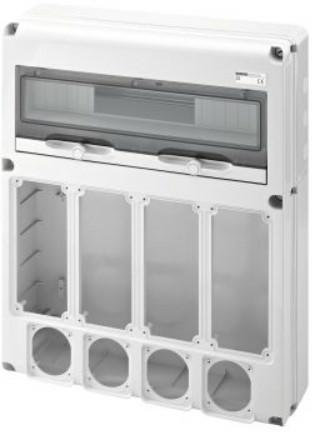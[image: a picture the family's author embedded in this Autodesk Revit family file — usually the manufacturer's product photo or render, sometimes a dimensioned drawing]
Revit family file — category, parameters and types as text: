
# Revit family: Building-IEC309Boards-GEWISS-68QDIN-DISTRIBUTION-BOARD-20MOD_4SOCKET-OUTLETS_IB_VERT_4SOCKET-OUTLETS
name_source: partatom
category: Apparecchi elettrici
units: mm (PartAtom-declared; Revit-internal decimal feet)

## family parameters
Condiviso = No
Host = Superficie
Mantenere orientamento annotazione = Sì
Punto di calcolo locali = Sì
Quota connettore circolare = Usa diametro
Taglio con vuoti quando caricato = No
Tipo di parte = Normale

## types (1)
- GW68015N - Q-DIN 20M 4S.O.BL.VR.SBF 4S.O.16A IP65
    Accordance with Standards = EN 60208 - EN 60670-1 - IEC 60670-24
    Catalogue = BUILDING
    Catalogue Range = 68 QDIN
    Colour = Grey RAL 7035
    Descrizione = Q-DIN 20M 4S.O.BL.VR.SBF 4S.O.16A IP65
    Dispersible power A (W) = 30
    Dispersible power B (W) = 92
    EAN code = 8011564744844
    Electrocod = 2242
    Glow Wire Test = 650°C
    Houseable socket = 4IB 16/32A IP67 + 4 IEC MAX 3P+E 16A
    IDF = 7c51f678-f399-4c5a-96c9-a6b5e9979826
    IDT = 5bb38b2c-aa49-47b5-9d7c-4db2ea1b42ab
    IP degree = IP65
    Immagine tipo = GW68015N.jpg
    Installation type = Surface-mounting
    Insulation class = II
    L_Moduli = 380 mm  [stored 1.24672 ft]
    Modello = GW68015N
    N_Moduli = 20 mm  [stored 0.0656168 ft]
    No. IB socket-outlets houseable = 4IB 16/32A IP67 + 4 IEC MAX 3P+E 16A
    No. of blank lids supplied = 2 IB 16/32A + 4 IEC 16A
    No. of modules EN 50022 = 20
    No. of provided blank lids = 2 IB 16/32A + 4 IEC 16A
    Operating temperature: = -25 +40 °C
    POMELLO = bianco
    PRESA = rosso
    Produttore = GEWISS S.p.A.
    Prospetto di default = 1219 mm
    SEO = Board
    STRUTTURA = RAL - 7035
    STRUTTURA ALTA = Poche
    Shock resistance = IK08
    Spostamento_S = 1000 mm  [stored 3.28084 ft]
    Technical sheet = https://www.gewiss.com
    Thermo-pressure with ball = 70
    URL = https://www.gewiss.com
    VETRO = Vetro
    Version file RFA = 21.5
    Version type = Empty
    Working temperature = -25 ÷ +40 °C

note: source unit labels omitted for Thermo-pressure with ball — the stored unit's dimension contradicts the parameter name (converter mislabeling)

note: [stored X ft] marks values corroborated as IEEE doubles in the binary element streams (Revit-internal decimal feet)

## geometry (parser evidence)
native form markers: Sweep x4
no freeform markers — native parametric forms only
